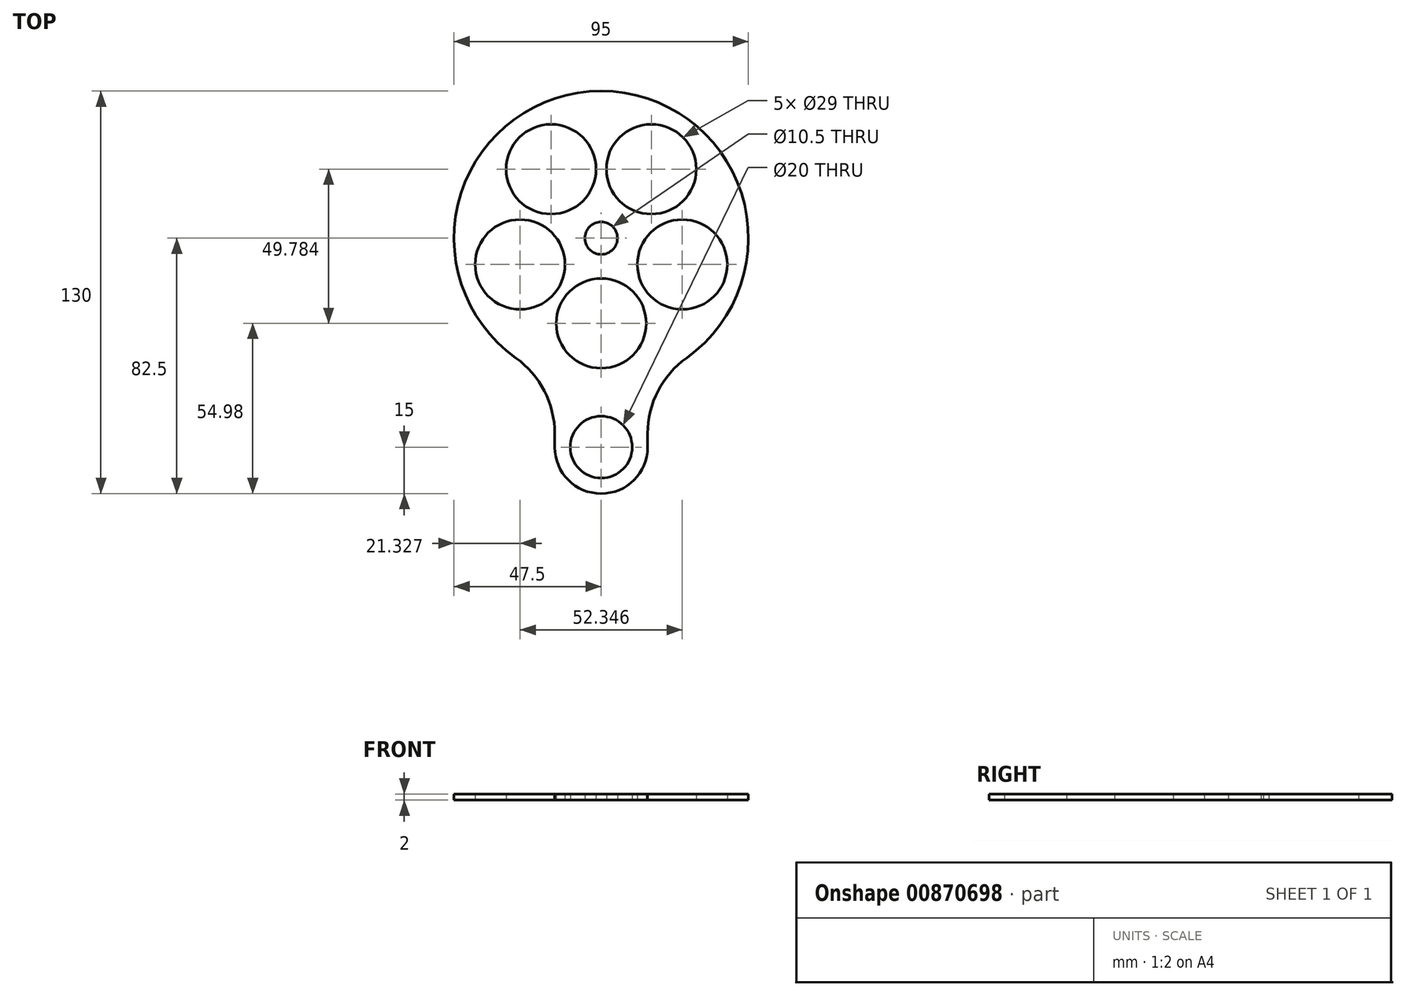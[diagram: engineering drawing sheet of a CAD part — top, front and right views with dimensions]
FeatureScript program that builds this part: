
annotation { "Feature Type Name" : "Feature", "Feature Type Description" : "" }
export const myFeature = defineFeature(function(context is Context, id is Id, definition is map)
    precondition{}
    {
        {
            var Q0;
            Q0=qCreatedBy(makeId("Top.planeOp"),FACE);
            var sketch = newSketch(context, id + "F0", { "sketchPlane" : qUnion([Q0])});
            skCircle(sketch, "E0", {"center": v(0, 0) * mm, "radius": 37 * mm});
            skCircle(sketch, "E1.cCircle", {"center": v(0, 0) * mm, "radius": 22.26 * mm, "construction": true});
            skLineSegment(sketch, "E1.0", {"start": v(26.17, -8.5) * mm, "end": v(0, -27.52) * mm, "construction": true});
            skLineSegment(sketch, "E1.1", {"start": v(0, -27.52) * mm, "end": v(-26.17, -8.5) * mm, "construction": true});
            skLineSegment(sketch, "E1.2", {"start": v(-26.17, -8.5) * mm, "end": v(-16.18, 22.26) * mm, "construction": true});
            skLineSegment(sketch, "E1.3", {"start": v(-16.18, 22.26) * mm, "end": v(16.18, 22.26) * mm, "construction": true});
            skLineSegment(sketch, "E1.4", {"start": v(16.18, 22.26) * mm, "end": v(26.17, -8.5) * mm, "construction": true});
            skPoint(sketch, "E1.0.midPoint", {"position": v(13.09, -18.01) * mm});
            skCircle(sketch, "E2", {"center": v(0, -27.52) * mm, "radius": 14.5 * mm});
            skCircle(sketch, "E3.cCircle", {"center": v(0, 0) * mm, "radius": 22.63 * mm, "construction": true});
            skLineSegment(sketch, "E3.0", {"start": v(26.6, -8.64) * mm, "end": v(0, -27.97) * mm, "construction": true});
            skLineSegment(sketch, "E3.1", {"start": v(0, -27.97) * mm, "end": v(-26.6, -8.64) * mm, "construction": true});
            skLineSegment(sketch, "E3.2", {"start": v(-26.6, -8.64) * mm, "end": v(-16.44, 22.63) * mm, "construction": true});
            skLineSegment(sketch, "E3.3", {"start": v(-16.44, 22.63) * mm, "end": v(16.44, 22.63) * mm, "construction": true});
            skLineSegment(sketch, "E3.4", {"start": v(16.44, 22.63) * mm, "end": v(26.6, -8.64) * mm, "construction": true});
            skPoint(sketch, "E3.0.midPoint", {"position": v(0, -22.63) * mm});
            skCircle(sketch, "E4.cCircle", {"center": v(0, 0) * mm, "radius": 23.26 * mm, "construction": true});
            skLineSegment(sketch, "E4.0", {"start": v(0, -28.76) * mm, "end": v(-27.35, -8.89) * mm, "construction": true});
            skLineSegment(sketch, "E4.1", {"start": v(-27.35, -8.89) * mm, "end": v(-16.9, 23.26) * mm, "construction": true});
            skLineSegment(sketch, "E4.2", {"start": v(-16.9, 23.26) * mm, "end": v(16.9, 23.26) * mm, "construction": true});
            skLineSegment(sketch, "E4.3", {"start": v(16.9, 23.26) * mm, "end": v(27.35, -8.89) * mm, "construction": true});
            skLineSegment(sketch, "E4.4", {"start": v(27.35, -8.89) * mm, "end": v(0, -28.76) * mm, "construction": true});
            skPoint(sketch, "E4.0.midPoint", {"position": v(-13.67, -18.82) * mm});
            skCircle(sketch, "E5.cCircle", {"center": v(0, 0) * mm, "radius": 23.91 * mm, "construction": true});
            skLineSegment(sketch, "E5.0", {"start": v(-28.11, -9.13) * mm, "end": v(-17.37, 23.91) * mm, "construction": true});
            skLineSegment(sketch, "E5.1", {"start": v(-17.37, 23.91) * mm, "end": v(17.37, 23.91) * mm, "construction": true});
            skLineSegment(sketch, "E5.2", {"start": v(17.37, 23.91) * mm, "end": v(28.11, -9.13) * mm, "construction": true});
            skLineSegment(sketch, "E5.3", {"start": v(28.11, -9.13) * mm, "end": v(0, -29.56) * mm, "construction": true});
            skLineSegment(sketch, "E5.4", {"start": v(0, -29.56) * mm, "end": v(-28.11, -9.13) * mm, "construction": true});
            skPoint(sketch, "E5.0.midPoint", {"position": v(-22.74, 7.39) * mm});
            skCircle(sketch, "E6.cCircle", {"center": v(0, 0) * mm, "radius": 24.68 * mm, "construction": true});
            skLineSegment(sketch, "E6.0", {"start": v(-17.93, 24.68) * mm, "end": v(17.93, 24.68) * mm, "construction": true});
            skLineSegment(sketch, "E6.1", {"start": v(17.93, 24.68) * mm, "end": v(29.02, -9.43) * mm, "construction": true});
            skLineSegment(sketch, "E6.2", {"start": v(29.02, -9.43) * mm, "end": v(0, -30.51) * mm, "construction": true});
            skLineSegment(sketch, "E6.3", {"start": v(0, -30.51) * mm, "end": v(-29.02, -9.43) * mm, "construction": true});
            skLineSegment(sketch, "E6.4", {"start": v(-29.02, -9.43) * mm, "end": v(-17.93, 24.68) * mm, "construction": true});
            skPoint(sketch, "E6.0.midPoint", {"position": v(0, 24.68) * mm});
            skCircle(sketch, "E7", {"center": v(-26.17, -8.5) * mm, "radius": 14.5 * mm});
            skCircle(sketch, "E8", {"center": v(-16.18, 22.26) * mm, "radius": 14.5 * mm});
            skCircle(sketch, "E9", {"center": v(16.18, 22.26) * mm, "radius": 14.5 * mm});
            skCircle(sketch, "E10", {"center": v(26.17, -8.5) * mm, "radius": 14.5 * mm});
            skCircle(sketch, "E11", {"center": v(0, 0) * mm, "radius": 5.25 * mm});
            skCircle(sketch, "E12", {"center": v(0, 0) * mm, "radius": 47.5 * mm});
            skCircle(sketch, "E13", {"center": v(0, -67.5) * mm, "radius": 10 * mm});
            skCircle(sketch, "E14", {"center": v(0, -67.5) * mm, "radius": 15 * mm});
            skLineSegment(sketch, "E15.bottom", {"start": v(-15, -67.5) * mm, "end": v(15, -67.5) * mm});
            skLineSegment(sketch, "E15.top", {"start": v(-15, -45.07) * mm, "end": v(15, -45.07) * mm});
            skLineSegment(sketch, "E15.left", {"start": v(-15, -67.5) * mm, "end": v(-15, -45.07) * mm});
            skLineSegment(sketch, "E15.right", {"start": v(15, -67.5) * mm, "end": v(15, -45.07) * mm});
            skSolve(sketch);
        }
        {
            var Q0;
            Q0=makeQuery(id+"F0.imprint","IMPRINT",FACE,{"disambiguationData":[TD([[makeQuery(id+"F0.imprint","IMPRINT",EDGE,{"derivedFrom":sQuery(id+"F0.wireOp",EDGE,"E11")}),-1.0]])]});
            var Q1;
            {var subQ0=sQuery(id+"F0.wireOp",EDGE,"E15.left");Q1=makeQuery(id+"F0.imprint","IMPRINT",FACE,{"disambiguationData":[TD([[makeQuery(id+"F0.imprint","IMPRINT",EDGE,{"derivedFrom":subQ0}),-1.0]])]});}
            var Q2;
            {var subQ16=sQuery(id+"F0.wireOp",EDGE,"E15.top");Q2=makeQuery(id+"F0.imprint","IMPRINT",FACE,{"disambiguationData":[TD([[makeQuery(id+"F0.imprint","IMPRINT",EDGE,{"derivedFrom":subQ16}),1.0]])]});}
            var Q3;
            {var subQ0=sQuery(id+"F0.wireOp",EDGE,"E15.top");Q3=makeQuery(id+"F0.imprint","IMPRINT",FACE,{"disambiguationData":[TD([[makeQuery(id+"F0.imprint","IMPRINT",EDGE,{"derivedFrom":subQ0}),-1.0]])]});}
            var Q4;
            {var subQ0=sQuery(id+"F0.wireOp",EDGE,"E15.bottom");var subQ1=sQuery(id+"F0.wireOp",EDGE,"E13");var subQ2=makeQuery(id+"F0.imprint","INTERSECT",VERTEX,{"disambiguationData":[OD(0.0)],"derivedFrom":[subQ1,subQ0]});Q4=makeQuery(id+"F0.imprint","IMPRINT",FACE,{"disambiguationData":[TD([[makeQuery(id+"F0.imprint","IMPRINT",EDGE,{"disambiguationData":[TD([[subQ2,1.0]])],"derivedFrom":subQ1}),-1.0]])]});}
            var Q5;
            {var subQ0=sQuery(id+"F0.wireOp",EDGE,"E15.bottom");var subQ1=sQuery(id+"F0.wireOp",EDGE,"E13");var subQ2=makeQuery(id+"F0.imprint","INTERSECT",VERTEX,{"disambiguationData":[OD(0.0)],"derivedFrom":[subQ1,subQ0]});Q5=makeQuery(id+"F0.imprint","IMPRINT",FACE,{"disambiguationData":[TD([[makeQuery(id+"F0.imprint","IMPRINT",EDGE,{"disambiguationData":[TD([[subQ2,-1.0]])],"derivedFrom":subQ1}),-1.0]])]});}
            extrude(context, id + "F1", {"entities" : qUnion([Q0, Q1, Q2, Q3, Q4, Q5]), "depth" : 2 * mm, "offsetDistance" : 25 * mm});
        }
        {
            var Q0;
            Q0=makeQuery(id+"F1.opExtrude","SWEPT_EDGE",EDGE,{"disambiguationData":[OSD([sQuery(id+"F0.wireOp",EDGE,"E12"),sQuery(id+"F0.wireOp",EDGE,"E15.top"),sQuery(id+"F0.wireOp",EDGE,"E15.right")])]});
            var Q1;
            Q1=makeQuery(id+"F1.opExtrude","SWEPT_EDGE",EDGE,{"disambiguationData":[OSD([sQuery(id+"F0.wireOp",EDGE,"E12"),sQuery(id+"F0.wireOp",EDGE,"E15.top"),sQuery(id+"F0.wireOp",EDGE,"E15.left")])]});
            fillet(context, id + "F2", {"entities" : qUnion([Q0, Q1]), "radius" : 30 * mm, "tangentPropagation" : true, "allowEdgeOverflow" : false});
        }
    });
